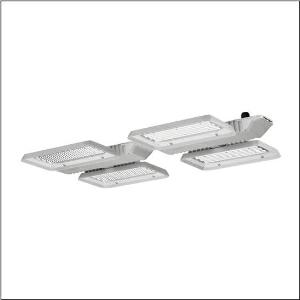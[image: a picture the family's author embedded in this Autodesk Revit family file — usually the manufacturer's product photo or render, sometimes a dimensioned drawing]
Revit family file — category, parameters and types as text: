
# Revit family: highbay_11_51hla2d24mca
name_source: partatom
category: Lighting Fixtures
units: mm (PartAtom-declared; Revit-internal decimal feet)

## family parameters
Cut with Voids When Loaded = No
Host = Face
Light Source = No
Part Type = Normal
Room Calculation Point = No
Round Connector Dimension = Use Diameter
Shared = No

## types (1)
- --- (1 x LED, 28800 lm, 162.4 W, 4000K)
    Apparent Load = 162 VA
    CIE Flux Codes = 89 96 99 100 100
    Color Rendering = 80
    Color Temperature = 4000K
    Default Elevation = 1800 mm
    Description = Highbay 11, LED high bay luminaire, primary light control with lens, of PMMA, light emission: direct distribution, primary light characteristic: symmetric, installation type: surface-mounted, suspended mounting, for 2x 2x LED, rated luminous flux: 28.800lm, luminous efficacy: 177lm/W, light colour: 840, colour temperature: 4000K, control gear: ECG DALI, with terminal, 5-pole, max. 2.5mm², mains connection: 230..240V, AC, 50/60Hz, rated input power: 162W, LED unit, of diecast aluminium, unplated, bead blasted, silver, length: 940mm, width: 500mm, height: 65mm, housing, of diecast aluminium, uncoated, bead blasted, silver, protection rating (complete): IP65, insulation class (complete): insulation class I (protective earthing), certification: CE, ENEC, VDE, UKCA, protection symbol: D, impact resistance: IK08 with glass or PC cover, permissible operating ambient temperature: -35..+55°C, reducing of maximum allowable ambient temperature of 5°C with ceiling mounting, corresponds to IFS (International Featured Standards) requirements for safety and quality in the food industry, packaging unit: 1 piece
    Height = 95 mm
    Lamp = 1 x LED
    Lamp Light Flux = 28800 lm
    Lamp Power = 162.4 W
    Lamp count = 1
    Length = 939 mm
    Luminous efficacy = 177 lm/W
    Manufacturer = Siteco
    ModVariant = No
    Model = 51HLA2D24MCA
    Mounting Place = Ceiling
    Mounting Type = Pendant
    Number of Poles = 1
    OnlyDefault = Yes
    Power Factor = 1
    Product Name = Highbay 11
    Product group = LED high bay luminaire
    ProductGroupID = 903
    Protection Class = Protection class I
    Protection Degree = IP 65
    RLX_Detail_Level = 1
    RLX_Emergency_Light_Flux = 0 lm
    RLX_Emergency_Type = 0
    RLX_Emergency_Type_DB = No
    RlxData = <blob elided: 96689 chars, md5=63596e6c>
    Socket = socket
    Standby Power = 0 W
    System Light Flux = 28800 lm
    System Power = 162 W
    Type Comments = factory setting: luminous flux: 100 % | dim-lin: 254 | 460 mA
    Type Image = l_1003428.jpg
    URL = http://relux.com
    VarID = @adj_177401
    Voltage = 0 V
    Weight = 0.00 kg
    Width = 501 mm

## geometry (parser evidence)
native form markers: Blend x4, Sweep x15
no freeform markers — native parametric forms only
